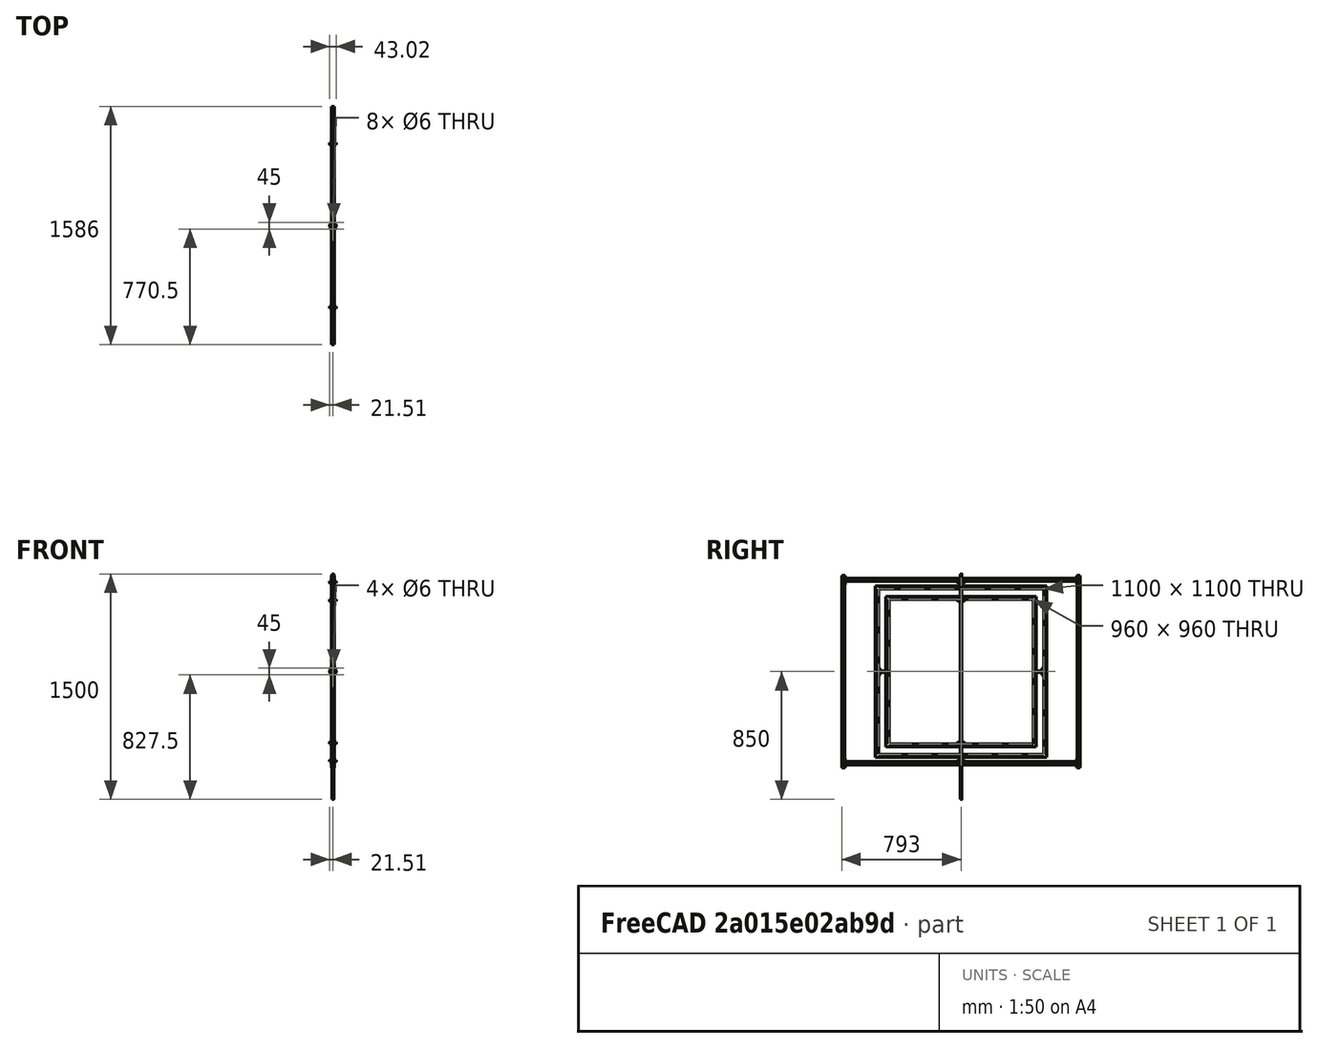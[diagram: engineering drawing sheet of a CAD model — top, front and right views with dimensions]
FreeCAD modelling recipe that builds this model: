
FCSTD DOCUMENT  (FreeCAD 0.20R25943 (Git))
Label: bancadaQuadrada
License: All rights reserved
LicenseURL: http://en.wikipedia.org/wiki/All_rights_reserved
objects: TechDraw::DrawViewDimension×19, Sketcher::SketchObject×14, Part::Extrusion×14, Part::Feature×5, TechDraw::DrawSVGTemplate×4, TechDraw::DrawViewPart×4, TechDraw::DrawPage×4, Part::Mirroring×3, Part::Cut×3, Part::Compound×2, Part::Fuse×1, PartDesign::Body×1, Part::Part2DObjectPython×1, Part::MultiFuse×1, TechDraw::DrawViewSymbol×1
note: 45 computed .brp shape members not serialized (recipe doc carries the construction recipe); baked Part::Feature solids carry a one-line shape summary decoded from their .brp

FEATURE [Sketcher::SketchObject] Sketch001
  FullyConstrained = true
  Placement = pos=(0,0,0) rot=(0.57735,0.57735,0.57735;2.0944rad)
  expr: Constraints[0] = Sketch.Constraints.espessura_arco
  sketch-geometry (9):
    g0: LineSegment StartX=550 StartY=-570 StartZ=0 EndX=570 EndY=-570 EndZ=0
    g1: LineSegment StartX=570 StartY=-570 StartZ=0 EndX=-570 EndY=-570 EndZ=0
    g2: LineSegment StartX=-570 StartY=-570 StartZ=0 EndX=-570 EndY=570 EndZ=0
    g3: LineSegment StartX=-570 StartY=570 StartZ=0 EndX=570 EndY=570 EndZ=0
    g4: LineSegment StartX=570 StartY=570 StartZ=0 EndX=570 EndY=-570 EndZ=0
    g5: LineSegment StartX=550 StartY=-550 StartZ=0 EndX=-550 EndY=-550 EndZ=0
    g6: LineSegment StartX=-550 StartY=-550 StartZ=0 EndX=-550 EndY=550 EndZ=0
    g7: LineSegment StartX=-550 StartY=550 StartZ=0 EndX=550 EndY=550 EndZ=0
    g8: LineSegment StartX=550 StartY=550 StartZ=0 EndX=550 EndY=-550 EndZ=0
  constraints (25):
    c: Distance(g0) = 20
    c: Coincident(g1,g2)
    c: Coincident(g2,g3)
    c: Coincident(g3,g4)
    c: Coincident(g4,g1)
    c: Horizontal(g1)
    c: Horizontal(g3)
    c: Vertical(g2)
    c: Vertical(g4)
    c: Coincident(g5,g6)
    c: Coincident(g6,g7)
    c: Coincident(g7,g8)
    c: Coincident(g8,g5)
    c: Horizontal(g5)
    c: Horizontal(g7)
    c: Vertical(g6)
    c: Vertical(g8)
    c: Equal(g7,g6)
    c: Equal(g2,g1)
    c: Symmetric(g7,g5,g-1)
    c: Symmetric(g1,g3,g-1)
    c: PointOnObject(g0,g8)
    c: Horizontal(g0)
    c: Distance(g5) = 1100
    c: Coincident(g0,g1)
FEATURE [Part::Extrusion] Extrude  label="arcoExterno"
  Base = -> Sketch001
  Dir = (1,0,0)
  DirMode = 2
  FaceMakerClass = Part::FaceMakerBullseye
  LengthFwd = 10
  LengthRev = 10
  Solid = true
  Symmetric = false
FEATURE [Sketcher::SketchObject] Sketch010
  FullyConstrained = true
  Placement = pos=(0,0,0) rot=(0.57735,0.57735,0.57735;2.0944rad)
  sketch-geometry (1):
    g0: Circle CenterX=0 CenterY=0 CenterZ=0 NormalX=0 NormalY=0 NormalZ=1 AngleXU=0 Radius=5
  constraints (2):
    c: Coincident(g0,g-1)
    c: Diameter(g0) = 10
FEATURE [Part::Extrusion] Extrude010
  Base = -> Sketch010
  Dir = (1,0,0)
  DirMode = 2
  FaceMakerClass = Part::FaceMakerBullseye
  LengthFwd = 1010
  LengthRev = 0
  Placement = pos=(0,0,0) rot=(0,1,0;1.5708rad)
  Solid = true
  Symmetric = true
FEATURE [Sketcher::SketchObject] Sketch011
  FullyConstrained = true
  Placement = pos=(0,0,0) rot=(0.57735,0.57735,0.57735;2.0944rad)
  sketch-geometry (8):
    g0: LineSegment StartX=-600 StartY=600 StartZ=0 EndX=600 EndY=600 EndZ=0
    g1: LineSegment StartX=600 StartY=600 StartZ=0 EndX=600 EndY=-600 EndZ=0
    g2: LineSegment StartX=600 StartY=-600 StartZ=0 EndX=-600 EndY=-600 EndZ=0
    g3: LineSegment StartX=-600 StartY=-600 StartZ=0 EndX=-600 EndY=600 EndZ=0
    g4: LineSegment StartX=-650 StartY=650 StartZ=0 EndX=650 EndY=650 EndZ=0
    g5: LineSegment StartX=650 StartY=650 StartZ=0 EndX=650 EndY=-650 EndZ=0
    g6: LineSegment StartX=650 StartY=-650 StartZ=0 EndX=-650 EndY=-650 EndZ=0
    g7: LineSegment StartX=-650 StartY=-650 StartZ=0 EndX=-650 EndY=650 EndZ=0
  constraints (22):
    c: Coincident(g0,g1)
    c: Coincident(g1,g2)
    c: Coincident(g2,g3)
    c: Coincident(g3,g0)
    c: Horizontal(g0)
    c: Horizontal(g2)
    c: Vertical(g1)
    c: Vertical(g3)
    c: Distance(g1) = 1200
    c: Equal(g2,g3)
    c: Symmetric(g0,g1,g-1)
    c: Coincident(g4,g5)
    c: Coincident(g5,g6)
    c: Coincident(g6,g7)
    c: Coincident(g7,g4)
    c: Horizontal(g4)
    c: Horizontal(g6)
    c: Vertical(g5)
    c: Vertical(g7)
    c: Equal(g4,g7)
    c: Symmetric(g5,g4,g-1)
    c: DistanceX(g4,g0) = 50
FEATURE [Sketcher::SketchObject] Sketch012
  FullyConstrained = true
  MapMode = 5
  Placement = pos=(0,0,650) rot=(0,0,1;0rad)
  sketch-geometry (1):
    g0: Circle CenterX=0 CenterY=0 CenterZ=0 NormalX=0 NormalY=0 NormalZ=1 AngleXU=0 Radius=5
  constraints (2):
    c: Diameter(g0) = 10
    c: Coincident(g-1,g0)
FEATURE [Part::Extrusion] Extrude012
  Base = -> Sketch012
  Dir = (0,0,-1)
  DirMode = 0
  FaceMakerClass = Part::FaceMakerBullseye
  LengthFwd = 1500
  LengthRev = 0
  Solid = true
  Symmetric = false
FEATURE [Sketcher::SketchObject] Sketch013
  FullyConstrained = true
  MapMode = 5
  Placement = pos=(0,0,-650) rot=(1,0,0;3.14159rad)
  sketch-geometry (1):
    g0: Circle CenterX=0 CenterY=0 CenterZ=0 NormalX=0 NormalY=0 NormalZ=1 AngleXU=0 Radius=5
  constraints (2):
    c: Coincident(g0,g-1)
    c: Diameter(g0) = 10
FEATURE [Part::Extrusion] Extrude013
  Base = -> Sketch013
  Dir = (0,0,1)
  DirMode = 0
  FaceMakerClass = Part::FaceMakerBullseye
  LengthFwd = 100
  LengthRev = 0
  Solid = true
  Symmetric = false
FEATURE [Part::Mirroring] Part__Mirroring  label="Extrude013 (Mirror #3)"
  Base = (0,0,0)
  Normal = (0,0,1)
  Source = -> Extrude013
FEATURE [Part::Compound] Compound
  Links = -> [Extrude013,Extrude,Part__Mirroring]
FEATURE [TechDraw::DrawSVGTemplate] Template001
  EditableTexts = Designed_by_Name=Bicudo; FC-Date=10/12/2021; FC-SC=1/10; FC-SH=Sheet; FC-Title=Bancada Drone; Subtitle=Quadros rotativos; Weight=Weight
  Height = 210
  Orientation = 1
  Width = 297
FEATURE [Sketcher::SketchObject] Sketch014
  FullyConstrained = false
  Placement = pos=(0,-550,-2.7e-14) rot=(0,0.707107,0.707107;3.14159rad)
  expr: Constraints[24] = .Constraints.angle
  expr: Constraints[25] = .Constraints.angle
  expr: Constraints[26] = .Constraints.angle
  sketch-geometry (12):
    g0: Circle CenterX=-8.3e-15 CenterY=-5.5 CenterZ=0 NormalX=0 NormalY=0 NormalZ=1 AngleXU=0 Radius=3
    g1: Circle CenterX=-8.3e-15 CenterY=-50.5 CenterZ=0 NormalX=0 NormalY=0 NormalZ=1 AngleXU=0 Radius=3
    g2: LineSegment StartX=-8.3e-15 StartY=-5.5 StartZ=0 EndX=-8.3e-15 EndY=-28 EndZ=0
    g3: LineSegment StartX=-8.3e-15 StartY=-28 StartZ=0 EndX=-8.3e-15 EndY=-50.5 EndZ=0
    g4: LineSegment StartX=-19.047 StartY=-18 StartZ=0 EndX=-7.5 EndY=2 EndZ=0
    g5: LineSegment StartX=-7.5 StartY=2 StartZ=0 EndX=7.5 EndY=2 EndZ=0
    g6: LineSegment StartX=7.5 StartY=2 StartZ=0 EndX=19.047 EndY=-18 EndZ=0
    g7: LineSegment StartX=-19.047 StartY=-38 StartZ=0 EndX=-7.5 EndY=-58 EndZ=0
    g8: LineSegment StartX=-7.5 StartY=-58 StartZ=0 EndX=7.5 EndY=-58 EndZ=0
    g9: LineSegment StartX=7.5 StartY=-58 StartZ=0 EndX=19.047 EndY=-38 EndZ=0
    g10: ArcOfCircle CenterX=-8.3e-15 CenterY=-28 CenterZ=0 NormalX=0 NormalY=0 NormalZ=1 AngleXU=0 Radius=21.5125 StartAngle=2.65813 EndAngle=3.62505
    g11: ArcOfCircle CenterX=-8.3e-15 CenterY=-28 CenterZ=0 NormalX=0 NormalY=0 NormalZ=1 AngleXU=0 Radius=21.5125 StartAngle=5.79973 EndAngle=6.76665
  constraints (32):
    c: Vertical(g0,g1)
    c: Coincident(g2,g0)
    c: Coincident(g3,g2)
    c: Coincident(g3,g1)
    c: Equal(g3,g2)
    c: Diameter(g1) = 6
    c: Equal(g1,g0)
    c: Distance(g0,g1) = 45
    c: Coincident(g4,g5)
    c: Coincident(g5,g6)
    c: Coincident(g7,g8)
    c: Coincident(g8,g9)
    c: Coincident(g10,g2)
    c: Coincident(g10,g7)
    c: Coincident(g10,g4)
    c: Coincident(g11,g10)
    c: Coincident(g11,g6)
    c: Coincident(g11,g9)
    c: Equal(g4,g6)
    c: Equal(g7,g9)
    c: Horizontal(g5)
    c: Horizontal(g8)
    c: DistanceY(g7,g4) = 60
    c: Angle(g4,g5) = 2.0944  'angle'
    c: Angle(g5,g6) = 2.0944
    c: Angle(g8,g7) = 2.0944
    c: Angle(g9,g8) = 2.0944
    c: Equal(g10,g11)
    c: Distance(g8) = 15
    c: Equal(g8,g5)
    c: Equal(g6,g7)
    c: DistanceY(g7,g7) = 20
FEATURE [Part::Extrusion] Extrude014
  Base = -> Sketch014
  Dir = (0,1,-2e-16)
  DirMode = 2
  FaceMakerClass = Part::FaceMakerBullseye
  LengthFwd = 5
  LengthRev = 0
  Solid = true
  Symmetric = false
FEATURE [Sketcher::SketchObject] Sketch015
  ExternalGeometry = -> [Sketch014]
  FullyConstrained = true
  Placement = pos=(-4.471e-12,-545,-28) rot=(-1,0,0;1.5708rad)
  sketch-geometry (1):
    g0: Circle CenterX=0 CenterY=0 CenterZ=0 NormalX=0 NormalY=0 NormalZ=1 AngleXU=0 Radius=21.5125
  constraints (2):
    c: Coincident(g0,g-1)
    c: Tangent(g0,g-3)
FEATURE [Part::Extrusion] Extrude015
  Base = -> Sketch015
  Dir = (0,1,2e-16)
  DirMode = 2
  FaceMakerClass = Part::FaceMakerBullseye
  LengthFwd = 7
  LengthRev = 0
  Solid = true
  Symmetric = false
FEATURE [Sketcher::SketchObject] Sketch016
  ExternalGeometry = -> [Sketch014]
  FullyConstrained = true
  Placement = pos=(-4.462e-12,-538,-28) rot=(-1,0,0;1.5708rad)
  sketch-geometry (2):
    g0: Circle CenterX=4.4699e-12 CenterY=-22.5 CenterZ=0 NormalX=0 NormalY=0 NormalZ=1 AngleXU=0 Radius=4
    g1: Circle CenterX=4.4713e-12 CenterY=22.5 CenterZ=0 NormalX=0 NormalY=0 NormalZ=1 AngleXU=0 Radius=4
  constraints (4):
    c: Coincident(g1,g-4)
    c: Coincident(g0,g-3)
    c: Equal(g1,g0)
    c: Diameter(g0) = 8
FEATURE [Part::Extrusion] Extrude016
  Base = -> Sketch016
  Dir = (0,-1,0)
  DirMode = 0
  FaceMakerClass = Part::FaceMakerBullseye
  LengthFwd = 10
  LengthRev = 0
  Solid = true
  Symmetric = false
FEATURE [Part::Cut] Cut007
  Base = -> Extrude015
  Tool = -> Extrude016
FEATURE [Part::Fuse] Fusion
  Base = -> Extrude014
  Placement = pos=(-4e-15,0,28) rot=(0,0,1;0rad)
  Tool = -> Cut007
FEATURE [Sketcher::SketchObject] Sketch
  FullyConstrained = true
  MapMode = 5
  Placement = pos=(0,0,0) rot=(0.57735,0.57735,0.57735;2.0944rad)
  Support = -> [YZ_Plane]
  sketch-geometry (10):
    g0: LineSegment StartX=-500 StartY=500 StartZ=0 EndX=500 EndY=500 EndZ=0
    g1: LineSegment StartX=500 StartY=500 StartZ=0 EndX=500 EndY=-500 EndZ=0
    g2: LineSegment StartX=500 StartY=-500 StartZ=0 EndX=-500 EndY=-500 EndZ=0
    g3: LineSegment StartX=-500 StartY=-500 StartZ=0 EndX=-500 EndY=500 EndZ=0
    g4: LineSegment StartX=-480 StartY=480 StartZ=0 EndX=480 EndY=480 EndZ=0
    g5: LineSegment StartX=480 StartY=480 StartZ=0 EndX=480 EndY=-480 EndZ=0
    g6: LineSegment StartX=480 StartY=-480 StartZ=0 EndX=-480 EndY=-480 EndZ=0
    g7: LineSegment StartX=-480 StartY=-480 StartZ=0 EndX=-480 EndY=480 EndZ=0
    g8: LineSegment StartX=-480 StartY=480 StartZ=0 EndX=-500 EndY=480 EndZ=0
    g9: LineSegment StartX=480 StartY=-480 StartZ=0 EndX=480 EndY=-500 EndZ=0
  constraints (28):
    c: Coincident(g0,g1)
    c: Coincident(g1,g2)
    c: Coincident(g2,g3)
    c: Coincident(g3,g0)
    c: Horizontal(g0)
    c: Horizontal(g2)
    c: Vertical(g1)
    c: Vertical(g3)
    c: Coincident(g4,g5)
    c: Coincident(g5,g6)
    c: Coincident(g6,g7)
    c: Coincident(g7,g4)
    c: Horizontal(g4)
    c: Horizontal(g6)
    c: Vertical(g5)
    c: Vertical(g7)
    c: Coincident(g8,g4)
    c: Horizontal(g8)
    c: Coincident(g5,g9)
    c: Perpendicular(g6,g9)
    c: Equal(g5,g6)
    c: Symmetric(g6,g4,g-1)
    c: PointOnObject(g8,g3)
    c: PointOnObject(g9,g2)
    c: Equal(g0,g3)
    c: Symmetric(g2,g0,g-1)
    c: Distance(g9) = 20  'espessura_arco'
    c: Distance(g2) = 1000
FEATURE [PartDesign::Body] Body
  Group = -> [Sketch001,Sketch]
  Origin = -> Origin
FEATURE [Part::Extrusion] Extrude017
  Base = -> Sketch
  Dir = (1,-1e-16,1e-16)
  DirMode = 2
  FaceMakerClass = Part::FaceMakerBullseye
  LengthFwd = 20
  LengthRev = 0
  Solid = true
  Symmetric = true
FEATURE [Sketcher::SketchObject] Sketch018
  ExternalGeometry = -> [Sketch001]
  FullyConstrained = true
  Placement = pos=(0,0,0) rot=(1,0,0;1.5708rad)
  sketch-geometry (1):
    g0: Circle CenterX=0 CenterY=0 CenterZ=0 NormalX=0 NormalY=0 NormalZ=1 AngleXU=0 Radius=5
  constraints (2):
    c: Coincident(g0,g-1)
    c: Diameter(g0) = 10
FEATURE [Part::Extrusion] Extrude018
  Base = -> Sketch018
  Dir = (0,-1,3e-16)
  DirMode = 2
  FaceMakerClass = Part::FaceMakerBullseye
  LengthFwd = 1100
  LengthRev = 0
  Solid = true
  Symmetric = true
FEATURE [Part::Part2DObjectPython] Rectangle  # Draft 2D object (typed FeaturePython)
  Area = 921600
  ChamferSize = 0
  Columns = 1
  FilletRadius = 0
  Height = 960
  Length = 960
  MakeFace = true
  Placement = pos=(10,-480,-480) rot=(0.57735,0.57735,0.57735;2.0944rad)
  Rows = 1
FEATURE [Part::Extrusion] Extrude019
  Base = -> Rectangle
  Dir = (1,0,0)
  DirMode = 2
  FaceMakerClass = Part::FaceMakerBullseye
  LengthFwd = 30
  LengthRev = 0
  Reversed = true
  Solid = false
  Symmetric = false
FEATURE [Part::Cut] Cut
  Base = -> Extrude018
  Tool = -> Extrude019
FEATURE [Part::Feature] Fusion_solid001  label="Fusion (Solid)001"
  Placement = pos=(0,0,0) rot=(1,0,0;3.14159rad)
  shape: bbox 43.03 x 12 x 60 mm, 23 faces (baked)
FEATURE [Part::Feature] Fusion_solid003  label="Fusion (Solid)003"
  Placement = pos=(9e-15,-1.35e-13,-50) rot=(1,0,0;1.5708rad)
  shape: bbox 43.03 x 60 x 12 mm, 23 faces (baked)
FEATURE [Part::Feature] Fusion_solid005  label="Fusion (Solid)005"
  Placement = pos=(8.9e-15,1.35e-13,50) rot=(-1,0,0;1.5708rad)
  shape: bbox 43.03 x 60 x 12 mm, 23 faces (baked)
FEATURE [Part::Feature] Fusion_solid007  label="Fusion (Solid)007"
  Placement = pos=(-4.4e-14,2.42e-13,-70) rot=(-1,0,0;1.5708rad)
  shape: bbox 43.03 x 60 x 12 mm, 23 faces (baked)
FEATURE [Part::Feature] Fusion_solid009  label="Fusion (Solid)009"
  Placement = pos=(6.2e-14,-2.42e-13,70) rot=(1,0,0;1.5708rad)
  shape: bbox 43.03 x 60 x 12 mm, 23 faces (baked)
FEATURE [TechDraw::DrawViewPart] View  label="Quadro interno"
  CoarseView = false
  Direction = (1,0,0)
  Focus = 100
  HardHidden = false
  IsoCount = 0
  IsoHidden = false
  IsoVisible = false
  LockPosition = false
  Perspective = false
  Rotation = 0
  Scale = 0.1
  ScaleType = 0
  SeamHidden = false
  SeamVisible = true
  SmoothHidden = false
  SmoothVisible = false
  Source = -> [Extrude017,Cut]
  X = 209.313
  XDirection = (0,1,0)
  Y = 141.348
FEATURE [TechDraw::DrawViewPart] View001  label="Quadro externo"
  CoarseView = false
  Direction = (1,0,0)
  Focus = 100
  HardHidden = false
  IsoCount = 0
  IsoHidden = false
  IsoVisible = false
  LockPosition = false
  Perspective = false
  Rotation = 0
  Scale = 0.1
  ScaleType = 0
  SeamHidden = false
  SeamVisible = true
  SmoothHidden = false
  SmoothVisible = true
  Source = -> [Compound]
  X = 88.0599
  XDirection = (0,1,0)
  Y = 127.31
FEATURE [TechDraw::DrawViewDimension] Dimension003
  Arbitrary = false
  ArbitraryTolerances = false
  EqualTolerance = true
  FormatSpec = %.2f
  FormatSpecOverTolerance = %+.2f
  FormatSpecUnderTolerance = %+.2f
  Inverted = false
  LockPosition = false
  MeasureType = 1
  OverTolerance = 0
  References2D = -> [View001]
  Rotation = 0
  Scale = 0.01
  ScaleType = 0
  TheoreticalExact = false
  Type = 2
  UnderTolerance = 0
  X = -71.2312
  Y = 13.1748
FEATURE [TechDraw::DrawViewDimension] Dimension004
  Arbitrary = false
  ArbitraryTolerances = false
  EqualTolerance = true
  FormatSpec = %.2f
  FormatSpecOverTolerance = %+.2f
  FormatSpecUnderTolerance = %+.2f
  Inverted = false
  LockPosition = false
  MeasureType = 1
  OverTolerance = 0
  References2D = -> [View001]
  Rotation = 0
  Scale = 0.01
  ScaleType = 0
  TheoreticalExact = false
  Type = 1
  UnderTolerance = 0
  X = -28.4406
  Y = -47.8032
FEATURE [TechDraw::DrawViewDimension] Dimension005
  Arbitrary = false
  ArbitraryTolerances = false
  EqualTolerance = true
  FormatSpec = %.2f
  FormatSpecOverTolerance = %+.2f
  FormatSpecUnderTolerance = %+.2f
  Inverted = false
  LockPosition = false
  MeasureType = 1
  OverTolerance = 0
  References2D = -> [View001]
  Rotation = 0
  Scale = 0.01
  ScaleType = 0
  TheoreticalExact = false
  Type = 2
  UnderTolerance = 0
  X = 37.2039
  Y = 5.58896
FEATURE [TechDraw::DrawViewDimension] Dimension
  Arbitrary = false
  ArbitraryTolerances = false
  EqualTolerance = true
  FormatSpec = %.2f
  FormatSpecOverTolerance = %+.2f
  FormatSpecUnderTolerance = %+.2f
  Inverted = false
  LockPosition = false
  MeasureType = 1
  OverTolerance = 0
  References2D = -> [View]
  Rotation = 0
  Scale = 0.01
  ScaleType = 0
  TheoreticalExact = false
  Type = 1
  UnderTolerance = 0
  X = 17.7394
  Y = 20.0313
FEATURE [TechDraw::DrawViewDimension] Dimension008
  Arbitrary = false
  ArbitraryTolerances = false
  EqualTolerance = true
  FormatSpec = %.2f
  FormatSpecOverTolerance = %+.2f
  FormatSpecUnderTolerance = %+.2f
  Inverted = false
  LockPosition = false
  MeasureType = 1
  OverTolerance = 0
  References2D = -> [View001]
  Rotation = 0
  Scale = 0.01
  ScaleType = 0
  TheoreticalExact = false
  Type = 1
  UnderTolerance = 0
  X = 3.25697
  Y = -79.1285
FEATURE [TechDraw::DrawViewDimension] Dimension009
  Arbitrary = false
  ArbitraryTolerances = false
  EqualTolerance = true
  FormatSpec = %.2f
  FormatSpecOverTolerance = %+.2f
  FormatSpecUnderTolerance = %+.2f
  Inverted = false
  LockPosition = false
  MeasureType = 1
  OverTolerance = 0
  References2D = -> [View]
  Rotation = 0
  Scale = 0.01
  ScaleType = 0
  TheoreticalExact = false
  Type = 1
  UnderTolerance = 0
  X = 7.54644
  Y = -76.5093
FEATURE [TechDraw::DrawViewDimension] Dimension010
  Arbitrary = false
  ArbitraryTolerances = false
  EqualTolerance = true
  FormatSpec = %.2f
  FormatSpecOverTolerance = %+.2f
  FormatSpecUnderTolerance = %+.2f
  Inverted = false
  LockPosition = false
  MeasureType = 1
  OverTolerance = 0
  References2D = -> [View]
  Rotation = 0
  Scale = 0.01
  ScaleType = 0
  TheoreticalExact = false
  Type = 2
  UnderTolerance = 0
  X = 64.1254
  Y = -7.54644
FEATURE [TechDraw::DrawViewDimension] Dimension011
  Arbitrary = false
  ArbitraryTolerances = false
  EqualTolerance = true
  FormatSpec = %.2f
  FormatSpecOverTolerance = %+.2f
  FormatSpecUnderTolerance = %+.2f
  Inverted = false
  LockPosition = false
  MeasureType = 1
  OverTolerance = 0
  References2D = -> [View001]
  Rotation = 0
  Scale = 0.01
  ScaleType = 0
  TheoreticalExact = false
  Type = 1
  UnderTolerance = 0
  X = -20.8018
  Y = 63.978
FEATURE [TechDraw::DrawViewDimension] Dimension012
  Arbitrary = false
  ArbitraryTolerances = false
  EqualTolerance = true
  FormatSpec = %.2f
  FormatSpecOverTolerance = %+.2f
  FormatSpecUnderTolerance = %+.2f
  Inverted = false
  LockPosition = false
  MeasureType = 1
  OverTolerance = 0
  References2D = -> [View]
  Rotation = 0
  Scale = 0.01
  ScaleType = 0
  TheoreticalExact = false
  Type = 2
  UnderTolerance = 0
  X = 32.4996
  Y = 8.23256
FEATURE [TechDraw::DrawViewDimension] Dimension013
  Arbitrary = false
  ArbitraryTolerances = false
  EqualTolerance = true
  FormatSpec = %.2f
  FormatSpecOverTolerance = %+.2f
  FormatSpecUnderTolerance = %+.2f
  Inverted = false
  LockPosition = false
  MeasureType = 1
  OverTolerance = 0
  References2D = -> [View]
  Rotation = 0
  Scale = 0.01
  ScaleType = 0
  TheoreticalExact = false
  Type = 2
  UnderTolerance = 0
  X = -35.9388
  Y = -23.0325
FEATURE [TechDraw::DrawViewDimension] Dimension014
  Arbitrary = false
  ArbitraryTolerances = false
  EqualTolerance = true
  FormatSpec = %.2f
  FormatSpecOverTolerance = %+.2f
  FormatSpecUnderTolerance = %+.2f
  Inverted = false
  LockPosition = false
  MeasureType = 1
  OverTolerance = 0
  References2D = -> [View001]
  Rotation = 0
  Scale = 0.01
  ScaleType = 0
  TheoreticalExact = false
  Type = 1
  UnderTolerance = 0
  X = 20.9175
  Y = -22.2481
FEATURE [TechDraw::DrawViewDimension] Dimension015
  Arbitrary = false
  ArbitraryTolerances = false
  EqualTolerance = true
  FormatSpec = %.2f
  FormatSpecOverTolerance = %+.2f
  FormatSpecUnderTolerance = %+.2f
  Inverted = false
  LockPosition = false
  MeasureType = 1
  OverTolerance = 0
  References2D = -> [View]
  Rotation = 0
  Scale = 0.01
  ScaleType = 0
  TheoreticalExact = false
  Type = 1
  UnderTolerance = 0
  X = -34.5108
  Y = 32.3963
FEATURE [Sketcher::SketchObject] Sketch020
  ExternalGeometry = -> [Extrude017,Fusion_solid005]
  FullyConstrained = true
  Placement = pos=(0,0,0) rot=(0.57735,0.57735,0.57735;2.0944rad)
  sketch-geometry (8):
    g0: LineSegment StartX=-750 StartY=-600 StartZ=0 EndX=-750 EndY=600 EndZ=0
    g1: LineSegment StartX=-750 StartY=600 StartZ=0 EndX=750 EndY=600 EndZ=0
    g2: LineSegment StartX=750 StartY=600 StartZ=0 EndX=750 EndY=-600 EndZ=0
    g3: LineSegment StartX=770 StartY=-620 StartZ=0 EndX=770 EndY=620 EndZ=0
    g4: LineSegment StartX=770 StartY=620 StartZ=0 EndX=-770 EndY=620 EndZ=0
    g5: LineSegment StartX=-770 StartY=620 StartZ=0 EndX=-770 EndY=-620 EndZ=0
    g6: LineSegment StartX=-750 StartY=-600 StartZ=0 EndX=750 EndY=-600 EndZ=0
    g7: LineSegment StartX=770 StartY=-620 StartZ=0 EndX=-770 EndY=-620 EndZ=0
  constraints (23):
    c: Vertical(g2)
    c: Vertical(g3)
    c: Coincident(g3,g4)
    c: Horizontal(g4)
    c: Coincident(g4,g5)
    c: Vertical(g5)
    c: Distance(g2) = 1200
    c: DistanceY(g1,g3) = 20
    c: Equal(g0,g2)
    c: Coincident(g0,g1)
    c: Vertical(g0)
    c: Coincident(g1,g2)
    c: PointOnObject(g0,g-4)
    c: Symmetric(g1,g0,g-2)
    c: Distance(g1) = 1500
    c: Coincident(g6,g0)
    c: Coincident(g6,g2)
    c: Coincident(g7,g3)
    c: Coincident(g7,g5)
    c: Horizontal(g7)
    c: DistanceY(g5,g0) = 20
    c: DistanceX(g5,g0) = 20
    c: DistanceX(g2,g3) = 20
FEATURE [Part::Extrusion] Extrude021
  Base = -> Sketch020
  Dir = (1,0,0)
  DirMode = 2
  FaceMakerClass = Part::FaceMakerBullseye
  LengthFwd = 20
  LengthRev = 0
  Solid = true
  Symmetric = true
FEATURE [Sketcher::SketchObject] Sketch021
  ExternalGeometry = -> [Extrude021]
  FullyConstrained = true
  Placement = pos=(0,0,0) rot=(0.57735,0.57735,0.57735;2.0944rad)
  sketch-geometry (4):
    g0: LineSegment StartX=-1000 StartY=600 StartZ=0 EndX=1000 EndY=600 EndZ=0
    g1: LineSegment StartX=1000 StartY=600 StartZ=0 EndX=1000 EndY=-600 EndZ=0
    g2: LineSegment StartX=1000 StartY=-600 StartZ=0 EndX=-1000 EndY=-600 EndZ=0
    g3: LineSegment StartX=-1000 StartY=-600 StartZ=0 EndX=-1000 EndY=600 EndZ=0
  constraints (11):
    c: Coincident(g0,g1)
    c: Coincident(g1,g2)
    c: Coincident(g2,g3)
    c: Coincident(g3,g0)
    c: Horizontal(g2)
    c: Vertical(g1)
    c: Vertical(g3)
    c: Distance(g0) = 2000
    c: Symmetric(g0,g0,g-2)
    c: PointOnObject(g-4,g2)
    c: PointOnObject(g-3,g0)
FEATURE [Part::Extrusion] Extrude022
  Base = -> Sketch021
  Dir = (1,0,0)
  DirMode = 2
  FaceMakerClass = Part::FaceMakerBullseye
  LengthFwd = 30
  LengthRev = 0
  Solid = true
  Symmetric = true
FEATURE [Part::Cut] Cut008
  Base = -> Extrude021
  Tool = -> Extrude022
FEATURE [Sketcher::SketchObject] Sketch022
  ExternalGeometry = -> [Cut008]
  FullyConstrained = true
  Placement = pos=(0,770,610) rot=(0,0.707107,0.707107;3.14159rad)
  sketch-geometry (8):
    g0: LineSegment StartX=-10 StartY=30 StartZ=0 EndX=10 EndY=30 EndZ=0
    g1: LineSegment StartX=10 StartY=30 StartZ=0 EndX=10 EndY=-30 EndZ=0
    g2: LineSegment StartX=10 StartY=-30 StartZ=0 EndX=-10 EndY=-30 EndZ=0
    g3: LineSegment StartX=-10 StartY=-30 StartZ=0 EndX=-10 EndY=30 EndZ=0
    g4: LineSegment StartX=-10 StartY=-1190 StartZ=0 EndX=10 EndY=-1190 EndZ=0
    g5: LineSegment StartX=10 StartY=-1190 StartZ=0 EndX=10 EndY=-1250 EndZ=0
    g6: LineSegment StartX=10 StartY=-1250 StartZ=0 EndX=-10 EndY=-1250 EndZ=0
    g7: LineSegment StartX=-10 StartY=-1250 StartZ=0 EndX=-10 EndY=-1190 EndZ=0
  constraints (24):
    c: Coincident(g0,g1)
    c: Coincident(g1,g2)
    c: Coincident(g2,g3)
    c: Coincident(g3,g0)
    c: Horizontal(g0)
    c: Horizontal(g2)
    c: Vertical(g1)
    c: Vertical(g3)
    c: Coincident(g4,g5)
    c: Coincident(g5,g6)
    c: Coincident(g6,g7)
    c: Coincident(g7,g4)
    c: Horizontal(g4)
    c: Horizontal(g6)
    c: Vertical(g5)
    c: Vertical(g7)
    c: PointOnObject(g-4,g5)
    c: PointOnObject(g-3,g7)
    c: Distance(g-4,g5) = 20
    c: Distance(g-4,g4) = 20
    c: PointOnObject(g-6,g1)
    c: PointOnObject(g-5,g3)
    c: Distance(g-5,g0) = 20
    c: Distance(g-5,g2) = 20
FEATURE [Part::Extrusion] Extrude023
  Base = -> Sketch022
  Dir = (0,1,-2e-16)
  DirMode = 2
  FaceMakerClass = Part::FaceMakerBullseye
  LengthFwd = 3
  LengthRev = 0
  Solid = true
  Symmetric = false
FEATURE [Part::Mirroring] Part__Mirroring001  label="Extrude023 (Mirror #2)"
  Base = (0,0,0)
  Normal = (0,1,0)
  Source = -> Extrude023
FEATURE [Part::MultiFuse] Fusion001
  Shapes = -> [Part__Mirroring001,Extrude023,Cut008]
FEATURE [Sketcher::SketchObject] Sketch023
  ExternalGeometry = -> [Fusion001]
  FullyConstrained = true
  Placement = pos=(0,-773,610) rot=(0,0.707107,-0.707107;3.14159rad)
  sketch-geometry (4):
    g0: LineSegment StartX=-10 StartY=1250 StartZ=0 EndX=10 EndY=1250 EndZ=0
    g1: LineSegment StartX=10 StartY=1250 StartZ=0 EndX=10 EndY=-30 EndZ=0
    g2: LineSegment StartX=10 StartY=-30 StartZ=0 EndX=-10 EndY=-30 EndZ=0
    g3: LineSegment StartX=-10 StartY=-30 StartZ=0 EndX=-10 EndY=1250 EndZ=0
  constraints (10):
    c: Coincident(g0,g1)
    c: Coincident(g1,g2)
    c: Coincident(g2,g3)
    c: Coincident(g3,g0)
    c: Horizontal(g0)
    c: Horizontal(g2)
    c: Vertical(g1)
    c: Vertical(g3)
    c: Coincident(g0,g-3)
    c: Coincident(g2,g-4)
FEATURE [Part::Extrusion] Extrude024
  Base = -> Sketch023
  Dir = (0,-1,-2e-16)
  DirMode = 2
  FaceMakerClass = Part::FaceMakerBullseye
  LengthFwd = 20
  LengthRev = 0
  Solid = true
  Symmetric = false
FEATURE [Part::Mirroring] Part__Mirroring002  label="Extrude024 (Mirror #3)"
  Base = (-7.1e-15,0,-1.137e-13)
  Normal = (0,1,-1.19209e-07)
  Source = -> Extrude024
FEATURE [Part::Compound] Compound001
  Links = -> [Part__Mirroring002,Extrude024]
FEATURE [TechDraw::DrawSVGTemplate] Template
  EditableTexts = Designed_by_Name=Designed by Name; Drawing_number=Drawing number; FC-Date=10/18/2021; FC-SC=Scale; FC-SH=Sheet; FC-Title=Title; Subtitle=Suportes externos; Weight=Weight
  Height = 210
  Orientation = 1
  Width = 297
FEATURE [TechDraw::DrawViewPart] View002  label="Suportes horizontais"
  CoarseView = true
  Direction = (1,0,0)
  Focus = 100
  HardHidden = false
  IsoCount = 0
  IsoHidden = false
  IsoVisible = false
  LockPosition = false
  Perspective = false
  Rotation = 0
  Scale = 0.1
  ScaleType = 0
  SeamHidden = false
  SeamVisible = true
  SmoothHidden = false
  SmoothVisible = true
  Source = -> [Fusion001]
  X = 103.243
  XDirection = (0,1,0)
  Y = 128.956
FEATURE [TechDraw::DrawViewDimension] Dimension016
  Arbitrary = false
  ArbitraryTolerances = false
  EqualTolerance = true
  FormatSpec = %.2f
  FormatSpecOverTolerance = %+.2f
  FormatSpecUnderTolerance = %+.2f
  Inverted = false
  LockPosition = false
  MeasureType = 1
  OverTolerance = 0
  References2D = -> [View]
  Rotation = 0
  Scale = 0.01
  ScaleType = 0
  TheoreticalExact = false
  Type = 0
  UnderTolerance = 0
  X = 0
  Y = 0
FEATURE [TechDraw::DrawPage] Page001
  KeepUpdated = true
  NextBalloonIndex = 1
  ProjectionType = 0
  Scale = 0.01
  Template = -> Template001
  Views = -> [View,View001,Dimension003,Dimension004,Dimension005,Dimension,Dimension008,Dimension009,Dimension010,Dimension011,Dimension012,Dimension013,Dimension014,Dimension015,Dimension016]
FEATURE [TechDraw::DrawViewDimension] Dimension017
  Arbitrary = false
  ArbitraryTolerances = false
  EqualTolerance = true
  FormatSpec = %.2f
  FormatSpecOverTolerance = %+.2f
  FormatSpecUnderTolerance = %+.2f
  Inverted = false
  LockPosition = false
  MeasureType = 1
  OverTolerance = 0
  References2D = -> [View002]
  Rotation = 0
  Scale = 0.01
  ScaleType = 0
  TheoreticalExact = false
  Type = 1
  UnderTolerance = 0
  X = -0.292561
  Y = -50.5885
FEATURE [TechDraw::DrawViewDimension] Dimension018
  Arbitrary = false
  ArbitraryTolerances = false
  EqualTolerance = true
  FormatSpec = %.2f
  FormatSpecOverTolerance = %+.2f
  FormatSpecUnderTolerance = %+.2f
  Inverted = false
  LockPosition = false
  MeasureType = 1
  OverTolerance = 0
  References2D = -> [View002]
  Rotation = 0
  Scale = 0.01
  ScaleType = 0
  TheoreticalExact = false
  Type = 1
  UnderTolerance = 0
  X = 92.3274
  Y = -43.7632
FEATURE [TechDraw::DrawViewDimension] Dimension019
  Arbitrary = false
  ArbitraryTolerances = false
  EqualTolerance = true
  FormatSpec = %.2f
  FormatSpecOverTolerance = %+.2f
  FormatSpecUnderTolerance = %+.2f
  Inverted = false
  LockPosition = false
  MeasureType = 1
  OverTolerance = 0
  References2D = -> [View002]
  Rotation = 0
  Scale = 0.01
  ScaleType = 0
  TheoreticalExact = false
  Type = 2
  UnderTolerance = 0
  X = 94.6551
  Y = -60.4355
FEATURE [TechDraw::DrawViewDimension] Dimension020
  Arbitrary = false
  ArbitraryTolerances = false
  EqualTolerance = true
  FormatSpec = %.2f
  FormatSpecOverTolerance = %+.2f
  FormatSpecUnderTolerance = %+.2f
  Inverted = false
  LockPosition = false
  MeasureType = 1
  OverTolerance = 0
  References2D = -> [View002]
  Rotation = 0
  Scale = 0.01
  ScaleType = 0
  TheoreticalExact = false
  Type = 2
  UnderTolerance = 0
  X = -67.6012
  Y = -82.29
FEATURE [TechDraw::DrawPage] Page
  KeepUpdated = true
  NextBalloonIndex = 1
  ProjectionType = 0
  Scale = 0.01
  Template = -> Template
  Views = -> [View002,Dimension017,Dimension018,Dimension019,Dimension020]
FEATURE [TechDraw::DrawSVGTemplate] Template002
  EditableTexts = Designed_by_Name=Designed by Name; Drawing_number=Drawing number; FC-Date=Date; FC-SC=Scale; FC-SH=Sheet; FC-Title=Title; Subtitle=Subtitle; Weight=Weight
  Height = 210
  Orientation = 1
  Width = 297
FEATURE [TechDraw::DrawViewPart] View003  label="Suportes Verticais"
  CoarseView = true
  Direction = (1,0,0)
  Focus = 100
  HardHidden = false
  IsoCount = 0
  IsoHidden = false
  IsoVisible = false
  LockPosition = false
  Perspective = false
  Rotation = 0
  Scale = 0.1
  ScaleType = 0
  SeamHidden = false
  SeamVisible = true
  SmoothHidden = false
  SmoothVisible = true
  Source = -> [Compound001]
  X = 112.348
  XDirection = (0,1,0)
  Y = 132.114
FEATURE [TechDraw::DrawViewDimension] Dimension021
  Arbitrary = false
  ArbitraryTolerances = false
  EqualTolerance = true
  FormatSpec = %.2f
  FormatSpecOverTolerance = %+.2f
  FormatSpecUnderTolerance = %+.2f
  Inverted = false
  LockPosition = false
  MeasureType = 1
  OverTolerance = 0
  References2D = -> [View003]
  Rotation = 0
  Scale = 0.01
  ScaleType = 0
  TheoreticalExact = false
  Type = 2
  UnderTolerance = 0
  X = -69.4135
  Y = -1.2133
FEATURE [TechDraw::DrawViewDimension] Dimension022
  Arbitrary = false
  ArbitraryTolerances = false
  EqualTolerance = true
  FormatSpec = %.2f
  FormatSpecOverTolerance = %+.2f
  FormatSpecUnderTolerance = %+.2f
  Inverted = false
  LockPosition = false
  MeasureType = 1
  OverTolerance = 0
  References2D = -> [View003]
  Rotation = 0
  Scale = 0.01
  ScaleType = 0
  TheoreticalExact = false
  Type = 1
  UnderTolerance = 0
  X = -52.9176
  Y = -64.5128
FEATURE [TechDraw::DrawPage] Page002
  KeepUpdated = true
  NextBalloonIndex = 1
  ProjectionType = 0
  Scale = 0.01
  Template = -> Template002
  Views = -> [View003,Dimension021,Dimension022]
FEATURE [TechDraw::DrawSVGTemplate] Template003
  EditableTexts = Designed_by_Name=Designed by Name; Drawing_number=Drawing number; FC-Date=Date; FC-SC=Scale; FC-SH=Sheet; FC-Title=Title; Subtitle=Subtitle; Weight=Weight
  Height = 210
  Orientation = 1
  Width = 297
FEATURE [TechDraw::DrawViewSymbol] ActiveView
  LockPosition = false
  Rotation = 0
  Scale = 0.5
  ScaleType = 2
  Symbol = <blob: 409453 chars omitted>
  X = 123.141
  Y = 118.894
FEATURE [TechDraw::DrawPage] Page003
  KeepUpdated = true
  NextBalloonIndex = 1
  ProjectionType = 0
  Scale = 0.01
  Template = -> Template003
  Views = -> [ActiveView]
